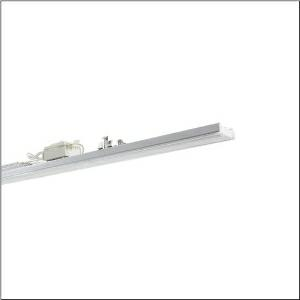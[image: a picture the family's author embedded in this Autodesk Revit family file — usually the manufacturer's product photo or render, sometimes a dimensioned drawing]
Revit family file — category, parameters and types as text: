
# Revit family: licross_r__11_recessed_mo_51tl12dv4fxgd_fd5d
name_source: partatom
category: Lighting Fixtures
units: mm (PartAtom-declared; Revit-internal decimal feet)

## family parameters
Cut with Voids When Loaded = No
Host = Face
Light Source = No
Part Type = Normal
Room Calculation Point = No
Round Connector Dimension = Use Diameter
Shared = No

## types (1)
- --- (1 x LED, 2300 lm, 12.5 W, 4000K)
    Apparent Load = 13 VA
    CIE Flux Codes = 67 92 99 100 100
    Color Rendering = 80
    Color Temperature = 4000K
    Default Elevation = 1800 mm
    Description = Licross® 11 Recessed MO, luminaire insert, of sheet steel, coil coated, white, length: 2.250mm, width: 66mm, height: 67mm, LED rated luminous flux: 15.360lm, light colour: 840, control gear: DALI 2 (for two DALI lines), with plug, 6-pole, with phase selection, mains connection: 220..240V, AC/DC, 0/50..60Hz, rated input power: 84W, without changeover relay, for emergency light function, for central battery installations according to DIN EN 60598-2-22, halogen-free wiring, primary optical cover: cover, of PMMA, light emission: direct distribution, primary light characteristic: symmetric, protection rating (complete): IP40, insulation class (complete): insulation class I (protective earthing), certification: CE, ENEC, VDE, UKCA, protection symbol: D if used in an environment without relevant dust loads with corresponding accessories, impact resistance: IK06, permissible ambient temperature for indoor applications: -25..+35°C, standard: EN 60598-2-22, corresponds to IFS (International Featured Standards) requirements for safety and quality in the food industry, reducing of maximum allowable ambient temperature of 5°C with ceiling mounting, LABS conformity tested according to VDMA 24364:2018-05, packaging unit: 1 piece
    Height = 58 mm
    Lamp = 1 x LED
    Lamp Light Flux = 2300 lm
    Lamp Power = 12.5 W
    Lamp count = 1
    Length = 2250 mm
    Luminous efficacy = 184 lm/W
    Manufacturer = Siteco
    ModVariant = No
    Model = 51TL12DV4FXGD
    Mounting Place = Ceiling
    Mounting Type = Pendant
    Number of Poles = 1
    OnlyDefault = Yes
    Power Factor = 1
    Product Name = Licross® 11 Recessed MO
    Product group = luminaire insert
    ProductGroupID = 902
    Protection Class = Protection class I
    Protection Degree = IP 40
    RLX_Detail_Level = 1
    RLX_Emergency_Light_Flux = 0 lm
    RLX_Emergency_Type = 0
    RLX_Emergency_Type_DB = No
    RlxData = <blob elided: 30077 chars, md5=d8c716f4>
    Socket = socket
    Standby Power = 0 W
    System Light Flux = 2300 lm
    System Power = 13 W
    Type Comments = : DC mode (central or group accumulator) initial emergency light level
    Type Image = l_1296930.jpg
    URL = http://relux.com
    VarID = @adj_087554
    Voltage = 0 V
    Weight = 0.00 kg
    Width = 66 mm

## geometry (parser evidence)
native form markers: Blend x4, Sweep x10
no freeform markers — native parametric forms only
